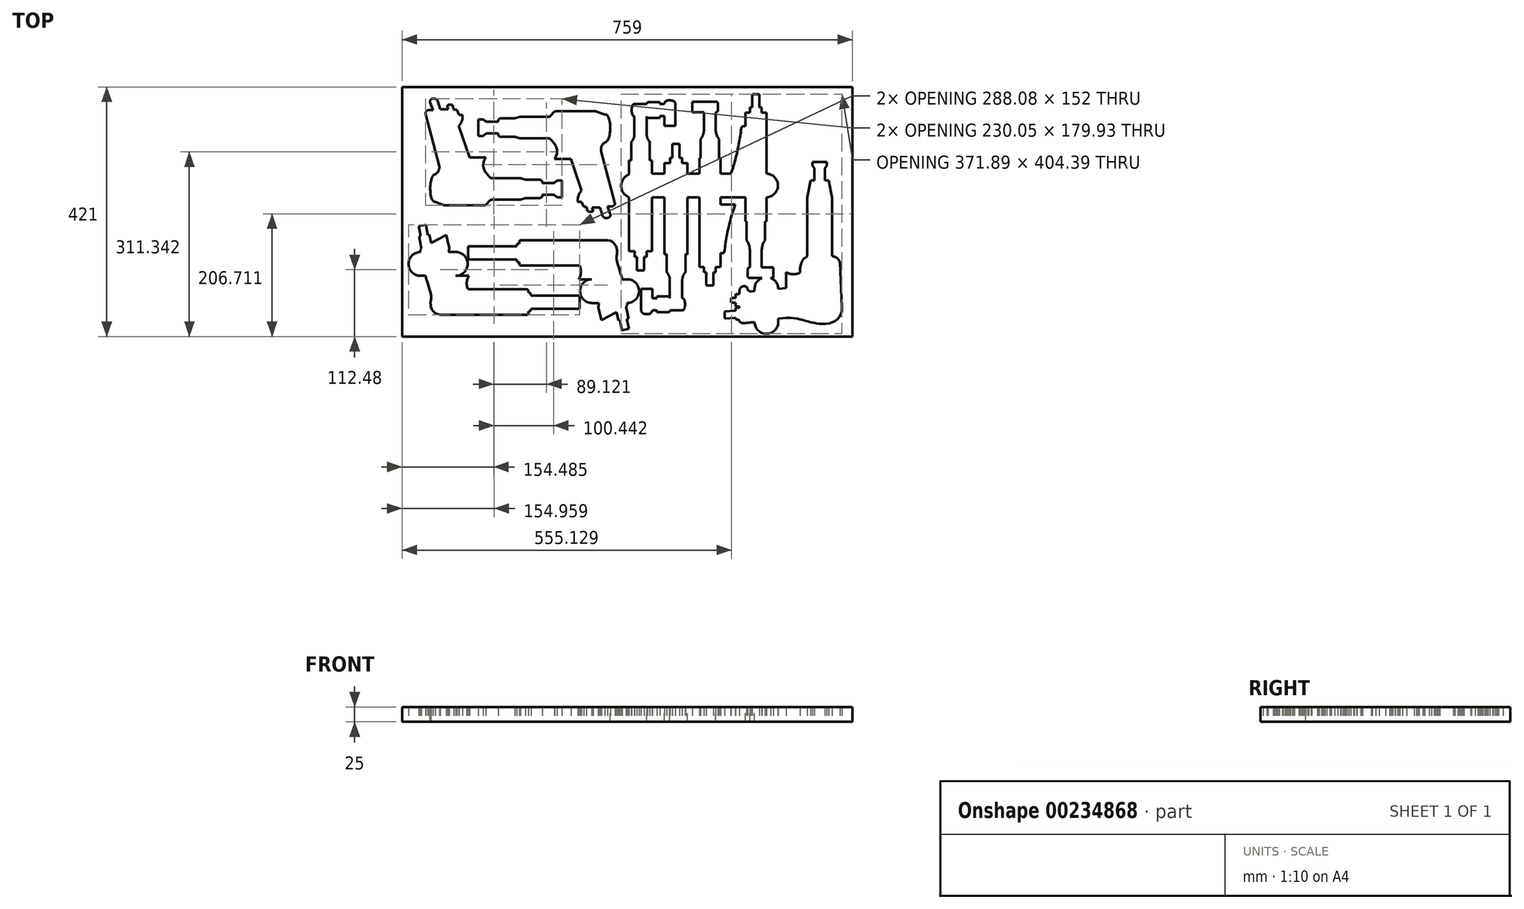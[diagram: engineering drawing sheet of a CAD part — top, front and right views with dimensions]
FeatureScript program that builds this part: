
annotation { "Feature Type Name" : "Feature", "Feature Type Description" : "" }
export const myFeature = defineFeature(function(context is Context, id is Id, definition is map)
    precondition{}
    {
        {
            var Q0;
            Q0=qCreatedBy(makeId("Top.planeOp"),FACE);
            var sketch = newSketch(context, id + "F0", { "sketchPlane" : qUnion([Q0])});
            skLineSegment(sketch, "E0.bottom", {"start": v(0, 0) * mm, "end": v(759, 0) * mm});
            skLineSegment(sketch, "E0.top", {"start": v(0, 421) * mm, "end": v(759, 421) * mm});
            skLineSegment(sketch, "E0.left", {"start": v(0, 0) * mm, "end": v(0, 421) * mm});
            skLineSegment(sketch, "E0.right", {"start": v(759, 0) * mm, "end": v(759, 421) * mm});
            skLineSegment(sketch, "E1", {"start": v(111, 79.48) * mm, "end": v(210, 79.48) * mm});
            skLineSegment(sketch, "E2", {"start": v(213, 76.48) * mm, "end": v(213, 73.79) * mm});
            skLineSegment(sketch, "E3", {"start": v(213, 73.79) * mm, "end": v(214, 73.79) * mm});
            skLineSegment(sketch, "E4", {"start": v(217, 70.79) * mm, "end": v(217, 68.98) * mm});
            skLineSegment(sketch, "E5", {"start": v(217, 68.98) * mm, "end": v(299, 68.98) * mm});
            skLineSegment(sketch, "E6", {"start": v(299, 68.98) * mm, "end": v(299, 57.98) * mm});
            skPoint(sketch, "E7.visualSharp", {"position": v(217, 73.79) * mm});
            skArc(sketch, "E7.filletArc", {"start": v(217, 70.79) * mm, "mid": v(216.12, 72.91) * mm, "end": v(214, 73.79) * mm});
            skPoint(sketch, "E8.visualSharp", {"position": v(213, 79.48) * mm});
            skArc(sketch, "E8.filletArc", {"start": v(213, 76.48) * mm, "mid": v(212.12, 78.6) * mm, "end": v(210, 79.48) * mm});
            skLineSegment(sketch, "E9", {"start": v(299, 57.98) * mm, "end": v(48, 57.98) * mm, "construction": true});
            skLineSegment(sketch, "E10.MirrorCS", {"start": v(217, 45.17) * mm, "end": v(217, 46.98) * mm});
            skLineSegment(sketch, "E11.MirrorCS", {"start": v(213, 39.48) * mm, "end": v(213, 42.17) * mm});
            skLineSegment(sketch, "E12.MirrorCS", {"start": v(213, 42.17) * mm, "end": v(214, 42.17) * mm});
            skArc(sketch, "E13.MirrorCS", {"start": v(213, 39.48) * mm, "mid": v(212.12, 37.36) * mm, "end": v(210, 36.48) * mm});
            skArc(sketch, "E14.MirrorCS", {"start": v(217, 45.17) * mm, "mid": v(216.12, 43.05) * mm, "end": v(214, 42.17) * mm});
            skPoint(sketch, "E15.MirrorP", {"position": v(213, 36.48) * mm});
            skLineSegment(sketch, "E16.MirrorCS", {"start": v(217, 46.98) * mm, "end": v(299, 46.98) * mm});
            skPoint(sketch, "E17.MirrorP", {"position": v(217, 42.17) * mm});
            skLineSegment(sketch, "E18.MirrorCS", {"start": v(111, 36.48) * mm, "end": v(210, 36.48) * mm});
            skLineSegment(sketch, "E19.MirrorCS", {"start": v(299, 46.98) * mm, "end": v(299, 57.98) * mm});
            skArc(sketch, "E20", {"start": v(111, 79.48) * mm, "mid": v(108.94, 91.17) * mm, "end": v(112.55, 102.48) * mm});
            skLineSegment(sketch, "E21", {"start": v(112.55, 102.48) * mm, "end": v(90.55, 102.48) * mm});
            skFitSpline(sketch, "E22", {"points": [v(90.55, 102.48) * mm, v(79.76, 149.3) * mm], "startDerivative": vector(-34.88, 29.55) * mm, "endDerivative": vector(11.44, 42.2) * mm});
            skLineSegment(sketch, "E23", {"start": v(111, 36.48) * mm, "end": v(64, 36.48) * mm});
            skFitSpline(sketch, "E24", {"points": [v(64, 36.48) * mm, v(48, 57.98) * mm, v(49, 67.48) * mm, v(30.64, 145.48) * mm], "startDerivative": vector(-146.18, 22.93) * mm, "endDerivative": vector(-15.62, 185.49) * mm});
            skLineSegment(sketch, "E25", {"start": v(30.64, 145.48) * mm, "end": v(32.76, 148.18) * mm});
            skLineSegment(sketch, "E26", {"start": v(48.76, 157.77) * mm, "end": v(74.25, 171.3) * mm});
            skLineSegment(sketch, "E27", {"start": v(74.25, 171.3) * mm, "end": v(79.76, 149.3) * mm});
            skLineSegment(sketch, "E28", {"start": v(28.24, 186.22) * mm, "end": v(40.02, 188.48) * mm});
            skLineSegment(sketch, "E29", {"start": v(40.02, 188.48) * mm, "end": v(43.32, 171.48) * mm});
            skLineSegment(sketch, "E30", {"start": v(43.32, 171.48) * mm, "end": v(46, 172) * mm});
            skLineSegment(sketch, "E31", {"start": v(46, 172) * mm, "end": v(48.76, 157.77) * mm});
            skLineSegment(sketch, "E32", {"start": v(28.24, 186.22) * mm, "end": v(31.5, 169.21) * mm});
            skLineSegment(sketch, "E33", {"start": v(31.5, 169.21) * mm, "end": v(28.83, 168.7) * mm});
            skLineSegment(sketch, "E34", {"start": v(28.83, 168.7) * mm, "end": v(32.76, 148.18) * mm});
            skLineSegment(sketch, "E35", {"start": v(28.83, 168.7) * mm, "end": v(43.32, 171.48) * mm, "construction": true});
            skLineSegment(sketch, "E36", {"start": v(49, 67.48) * mm, "end": v(49, 95.92) * mm, "construction": true});
            skLineSegment(sketch, "E37", {"start": v(49, 95.92) * mm, "end": v(49, 42.53) * mm, "construction": true});
            skLineSegment(sketch, "E38", {"start": v(299.36, 119.52) * mm, "end": v(200.36, 119.52) * mm});
            skLineSegment(sketch, "E39", {"start": v(197.36, 122.52) * mm, "end": v(197.36, 125.22) * mm});
            skLineSegment(sketch, "E40", {"start": v(197.36, 125.22) * mm, "end": v(196.36, 125.22) * mm});
            skLineSegment(sketch, "E41", {"start": v(193.36, 128.22) * mm, "end": v(193.36, 130.02) * mm});
            skLineSegment(sketch, "E42", {"start": v(193.36, 130.02) * mm, "end": v(111.36, 130.02) * mm});
            skLineSegment(sketch, "E43", {"start": v(111.36, 130.02) * mm, "end": v(111.36, 141.02) * mm});
            skPoint(sketch, "E44.visualSharp", {"position": v(193.36, 125.22) * mm});
            skArc(sketch, "E44.filletArc", {"start": v(193.36, 128.22) * mm, "mid": v(194.24, 126.1) * mm, "end": v(196.36, 125.22) * mm});
            skPoint(sketch, "E45.visualSharp", {"position": v(197.36, 119.52) * mm});
            skArc(sketch, "E45.filletArc", {"start": v(197.36, 122.52) * mm, "mid": v(198.24, 120.4) * mm, "end": v(200.36, 119.52) * mm});
            skLineSegment(sketch, "E46", {"start": v(111.36, 141.02) * mm, "end": v(362.36, 141.02) * mm, "construction": true});
            skLineSegment(sketch, "E47.MirrorCS", {"start": v(193.36, 153.83) * mm, "end": v(193.36, 152.02) * mm});
            skLineSegment(sketch, "E48.MirrorCS", {"start": v(197.36, 159.52) * mm, "end": v(197.36, 156.83) * mm});
            skLineSegment(sketch, "E49.MirrorCS", {"start": v(197.36, 156.83) * mm, "end": v(196.36, 156.83) * mm});
            skArc(sketch, "E50.MirrorCS", {"start": v(197.36, 159.52) * mm, "mid": v(198.24, 161.65) * mm, "end": v(200.36, 162.52) * mm});
            skArc(sketch, "E51.MirrorCS", {"start": v(193.36, 153.83) * mm, "mid": v(194.24, 155.95) * mm, "end": v(196.36, 156.83) * mm});
            skLineSegment(sketch, "E52.MirrorCS", {"start": v(193.36, 152.02) * mm, "end": v(111.36, 152.02) * mm});
            skPoint(sketch, "E53.MirrorP", {"position": v(193.36, 156.83) * mm});
            skLineSegment(sketch, "E54.MirrorCS", {"start": v(299.36, 162.52) * mm, "end": v(200.36, 162.52) * mm});
            skLineSegment(sketch, "E55.MirrorCS", {"start": v(111.36, 152.02) * mm, "end": v(111.36, 141.02) * mm});
            skArc(sketch, "E56", {"start": v(299.36, 119.52) * mm, "mid": v(301.42, 107.83) * mm, "end": v(297.8, 96.52) * mm});
            skLineSegment(sketch, "E57", {"start": v(297.8, 96.52) * mm, "end": v(319.8, 96.52) * mm});
            skFitSpline(sketch, "E58", {"points": [v(319.8, 96.52) * mm, v(330.6, 49.7) * mm], "startDerivative": vector(34.88, -29.55) * mm, "endDerivative": vector(-11.44, -42.2) * mm});
            skLineSegment(sketch, "E59", {"start": v(299.36, 162.52) * mm, "end": v(346.36, 162.52) * mm});
            skFitSpline(sketch, "E60", {"points": [v(346.36, 162.52) * mm, v(362.36, 141.02) * mm, v(361.36, 131.52) * mm, v(379.72, 53.52) * mm], "startDerivative": vector(146.18, -22.93) * mm, "endDerivative": vector(15.62, -185.49) * mm});
            skLineSegment(sketch, "E61", {"start": v(379.72, 53.52) * mm, "end": v(377.6, 50.82) * mm});
            skLineSegment(sketch, "E62", {"start": v(361.6, 41.24) * mm, "end": v(336.11, 27.7) * mm});
            skLineSegment(sketch, "E63", {"start": v(336.11, 27.7) * mm, "end": v(330.6, 49.7) * mm});
            skLineSegment(sketch, "E64", {"start": v(382.12, 12.79) * mm, "end": v(370.34, 10.52) * mm});
            skLineSegment(sketch, "E65", {"start": v(370.34, 10.52) * mm, "end": v(367.04, 27.52) * mm});
            skLineSegment(sketch, "E66", {"start": v(367.04, 27.52) * mm, "end": v(364.36, 27) * mm});
            skLineSegment(sketch, "E67", {"start": v(364.36, 27) * mm, "end": v(361.6, 41.24) * mm});
            skLineSegment(sketch, "E68", {"start": v(382.12, 12.79) * mm, "end": v(378.86, 29.79) * mm});
            skLineSegment(sketch, "E69", {"start": v(378.86, 29.79) * mm, "end": v(381.54, 30.3) * mm});
            skLineSegment(sketch, "E70", {"start": v(381.54, 30.3) * mm, "end": v(377.6, 50.82) * mm});
            skLineSegment(sketch, "E71", {"start": v(381.54, 30.3) * mm, "end": v(367.04, 27.52) * mm, "construction": true});
            skLineSegment(sketch, "E72", {"start": v(361.36, 131.52) * mm, "end": v(361.36, 103.09) * mm, "construction": true});
            skLineSegment(sketch, "E73", {"start": v(361.36, 103.09) * mm, "end": v(361.36, 156.48) * mm, "construction": true});
            skLineSegment(sketch, "E74", {"start": v(325.7, 379.95) * mm, "end": v(259.34, 379.95) * mm});
            skLineSegment(sketch, "E75", {"start": v(255.51, 378.17) * mm, "end": v(250.63, 372.35) * mm});
            skLineSegment(sketch, "E76", {"start": v(246.8, 370.56) * mm, "end": v(198.39, 370.56) * mm});
            skLineSegment(sketch, "E77", {"start": v(198.39, 370.56) * mm, "end": v(190.27, 368) * mm});
            skLineSegment(sketch, "E78", {"start": v(190.27, 368) * mm, "end": v(166.77, 368) * mm});
            skLineSegment(sketch, "E79", {"start": v(161.77, 363) * mm, "end": v(161.77, 362.07) * mm});
            skLineSegment(sketch, "E80", {"start": v(161.77, 362.07) * mm, "end": v(143.75, 362.07) * mm});
            skLineSegment(sketch, "E81", {"start": v(140.54, 363.24) * mm, "end": v(138.2, 365.2) * mm});
            skLineSegment(sketch, "E82", {"start": v(134.99, 366.37) * mm, "end": v(128.58, 366.37) * mm});
            skLineSegment(sketch, "E83", {"start": v(128.58, 366.37) * mm, "end": v(128.58, 352.34) * mm});
            skLineSegment(sketch, "E84", {"start": v(128.58, 352.34) * mm, "end": v(350.7, 352.34) * mm, "construction": true});
            skLineSegment(sketch, "E85", {"start": v(327.34, 379.67) * mm, "end": v(342.03, 374.55) * mm});
            skLineSegment(sketch, "E86.MirrorCS", {"start": v(128.58, 338.3) * mm, "end": v(128.58, 352.34) * mm});
            skLineSegment(sketch, "E87.MirrorCS", {"start": v(134.99, 338.3) * mm, "end": v(128.58, 338.3) * mm});
            skLineSegment(sketch, "E88.MirrorCS", {"start": v(140.54, 341.43) * mm, "end": v(138.2, 339.48) * mm});
            skLineSegment(sketch, "E89.MirrorCS", {"start": v(161.77, 342.6) * mm, "end": v(143.75, 342.6) * mm});
            skLineSegment(sketch, "E90.MirrorCS", {"start": v(161.77, 341.68) * mm, "end": v(161.77, 342.6) * mm});
            skLineSegment(sketch, "E91.MirrorCS", {"start": v(190.27, 336.68) * mm, "end": v(166.77, 336.68) * mm});
            skLineSegment(sketch, "E92.MirrorCS", {"start": v(198.39, 334.1) * mm, "end": v(190.27, 336.68) * mm});
            skLineSegment(sketch, "E93.MirrorCS", {"start": v(246.8, 334.1) * mm, "end": v(198.39, 334.1) * mm});
            skLineSegment(sketch, "E94.MirrorCS", {"start": v(257.01, 324.72) * mm, "end": v(250.63, 332.32) * mm});
            skArc(sketch, "E95", {"start": v(257.01, 324.72) * mm, "mid": v(261.18, 312.01) * mm, "end": v(256.9, 299.34) * mm});
            skLineSegment(sketch, "E96", {"start": v(256.9, 299.34) * mm, "end": v(284.3, 299.34) * mm});
            skLineSegment(sketch, "E97", {"start": v(284.3, 299.34) * mm, "end": v(302.62, 246.15) * mm});
            skArc(sketch, "E98", {"start": v(302.62, 246.15) * mm, "mid": v(297.24, 237.45) * mm, "end": v(296.27, 227.26) * mm});
            skLineSegment(sketch, "E99", {"start": v(358.47, 225.86) * mm, "end": v(335.71, 312.38) * mm});
            skArc(sketch, "E100", {"start": v(335.71, 312.38) * mm, "mid": v(336.3, 321.05) * mm, "end": v(342.03, 327.6) * mm});
            skLineSegment(sketch, "E101", {"start": v(342.03, 327.6) * mm, "end": v(342.03, 374.55) * mm, "construction": true});
            skFitSpline(sketch, "E102", {"points": [v(342.03, 327.6) * mm, v(342.03, 374.55) * mm], "startDerivative": vector(32.61, 0) * mm, "endDerivative": vector(-36.84, 0) * mm});
            skPoint(sketch, "E103.visualSharp", {"position": v(161.77, 336.68) * mm});
            skArc(sketch, "E103.filletArc", {"start": v(161.77, 341.68) * mm, "mid": v(163.23, 338.15) * mm, "end": v(166.77, 336.68) * mm});
            skPoint(sketch, "E104.visualSharp", {"position": v(161.77, 368) * mm});
            skArc(sketch, "E104.filletArc", {"start": v(166.77, 368) * mm, "mid": v(163.23, 366.53) * mm, "end": v(161.77, 363) * mm});
            skPoint(sketch, "E105.visualSharp", {"position": v(141.93, 342.6) * mm});
            skArc(sketch, "E105.filletArc", {"start": v(143.75, 342.6) * mm, "mid": v(142.04, 342.3) * mm, "end": v(140.54, 341.43) * mm});
            skPoint(sketch, "E106.visualSharp", {"position": v(136.8, 338.3) * mm});
            skArc(sketch, "E106.filletArc", {"start": v(134.99, 338.3) * mm, "mid": v(136.7, 338.6) * mm, "end": v(138.2, 339.48) * mm});
            skPoint(sketch, "E107.visualSharp", {"position": v(141.93, 362.07) * mm});
            skArc(sketch, "E107.filletArc", {"start": v(140.54, 363.24) * mm, "mid": v(142.04, 362.37) * mm, "end": v(143.75, 362.07) * mm});
            skPoint(sketch, "E108.visualSharp", {"position": v(136.8, 366.37) * mm});
            skArc(sketch, "E108.filletArc", {"start": v(138.2, 365.2) * mm, "mid": v(136.7, 366.06) * mm, "end": v(134.99, 366.37) * mm});
            skPoint(sketch, "E109.visualSharp", {"position": v(257.01, 379.95) * mm});
            skArc(sketch, "E109.filletArc", {"start": v(259.34, 379.95) * mm, "mid": v(257.23, 379.48) * mm, "end": v(255.51, 378.17) * mm});
            skPoint(sketch, "E110.visualSharp", {"position": v(249.13, 370.56) * mm});
            skArc(sketch, "E110.filletArc", {"start": v(246.8, 370.56) * mm, "mid": v(248.92, 371.03) * mm, "end": v(250.63, 372.35) * mm});
            skPoint(sketch, "E111.visualSharp", {"position": v(249.13, 334.1) * mm});
            skArc(sketch, "E111.filletArc", {"start": v(250.63, 332.32) * mm, "mid": v(248.92, 333.64) * mm, "end": v(246.8, 334.1) * mm});
            skPoint(sketch, "E112.visualSharp", {"position": v(326.54, 379.95) * mm});
            skArc(sketch, "E112.filletArc", {"start": v(327.34, 379.67) * mm, "mid": v(326.53, 379.88) * mm, "end": v(325.7, 379.95) * mm});
            skLineSegment(sketch, "E113", {"start": v(296.27, 227.26) * mm, "end": v(302.12, 227.26) * mm});
            skLineSegment(sketch, "E114", {"start": v(302.12, 227.26) * mm, "end": v(305.95, 218.52) * mm});
            skLineSegment(sketch, "E115", {"start": v(305.95, 218.52) * mm, "end": v(310.7, 218.52) * mm});
            skLineSegment(sketch, "E116", {"start": v(310.7, 218.52) * mm, "end": v(312.74, 212.03) * mm});
            skLineSegment(sketch, "E117", {"start": v(314.64, 210.63) * mm, "end": v(319.79, 210.63) * mm});
            skLineSegment(sketch, "E118", {"start": v(321.71, 213.17) * mm, "end": v(320.4, 217.85) * mm});
            skLineSegment(sketch, "E119", {"start": v(320.4, 217.85) * mm, "end": v(333.71, 217.85) * mm});
            skLineSegment(sketch, "E120", {"start": v(333.71, 217.85) * mm, "end": v(338.25, 203.51) * mm});
            skLineSegment(sketch, "E121", {"start": v(343.02, 200.02) * mm, "end": v(346.05, 200.02) * mm});
            skLineSegment(sketch, "E122", {"start": v(350.77, 206.68) * mm, "end": v(346.2, 219.59) * mm});
            skLineSegment(sketch, "E123", {"start": v(346.2, 219.59) * mm, "end": v(353.63, 219.59) * mm});
            skPoint(sketch, "E124.visualSharp", {"position": v(360.12, 219.59) * mm});
            skArc(sketch, "E124.filletArc", {"start": v(353.63, 219.59) * mm, "mid": v(357.6, 221.54) * mm, "end": v(358.47, 225.86) * mm});
            skPoint(sketch, "E125.visualSharp", {"position": v(353.12, 200.02) * mm});
            skArc(sketch, "E125.filletArc", {"start": v(346.05, 200.02) * mm, "mid": v(350.13, 202.13) * mm, "end": v(350.77, 206.68) * mm});
            skPoint(sketch, "E126.visualSharp", {"position": v(339.35, 200.02) * mm});
            skArc(sketch, "E126.filletArc", {"start": v(338.25, 203.51) * mm, "mid": v(340.06, 200.99) * mm, "end": v(343.02, 200.02) * mm});
            skPoint(sketch, "E127.visualSharp", {"position": v(322.43, 210.63) * mm});
            skArc(sketch, "E127.filletArc", {"start": v(319.79, 210.63) * mm, "mid": v(321.38, 211.42) * mm, "end": v(321.71, 213.17) * mm});
            skPoint(sketch, "E128.visualSharp", {"position": v(313.18, 210.63) * mm});
            skArc(sketch, "E128.filletArc", {"start": v(312.74, 212.03) * mm, "mid": v(313.46, 211.01) * mm, "end": v(314.64, 210.63) * mm});
            skLineSegment(sketch, "E129", {"start": v(72.4, 221.38) * mm, "end": v(138.75, 221.38) * mm});
            skLineSegment(sketch, "E130", {"start": v(142.58, 223.16) * mm, "end": v(147.46, 228.98) * mm});
            skLineSegment(sketch, "E131", {"start": v(151.29, 230.76) * mm, "end": v(199.7, 230.76) * mm});
            skLineSegment(sketch, "E132", {"start": v(199.7, 230.76) * mm, "end": v(207.83, 233.34) * mm});
            skLineSegment(sketch, "E133", {"start": v(207.83, 233.34) * mm, "end": v(231.33, 233.34) * mm});
            skLineSegment(sketch, "E134", {"start": v(236.33, 238.34) * mm, "end": v(236.33, 239.26) * mm});
            skLineSegment(sketch, "E135", {"start": v(236.33, 239.26) * mm, "end": v(254.34, 239.26) * mm});
            skLineSegment(sketch, "E136", {"start": v(257.55, 238.1) * mm, "end": v(259.89, 236.13) * mm});
            skLineSegment(sketch, "E137", {"start": v(263.1, 234.96) * mm, "end": v(269.5, 234.96) * mm});
            skLineSegment(sketch, "E138", {"start": v(269.5, 234.96) * mm, "end": v(269.5, 249) * mm});
            skLineSegment(sketch, "E139", {"start": v(269.5, 249) * mm, "end": v(47.38, 249) * mm, "construction": true});
            skLineSegment(sketch, "E140", {"start": v(70.75, 221.65) * mm, "end": v(56.06, 226.78) * mm});
            skLineSegment(sketch, "E141.MirrorCS", {"start": v(269.5, 263.02) * mm, "end": v(269.5, 249) * mm});
            skLineSegment(sketch, "E142.MirrorCS", {"start": v(263.1, 263.02) * mm, "end": v(269.5, 263.02) * mm});
            skLineSegment(sketch, "E143.MirrorCS", {"start": v(257.55, 259.9) * mm, "end": v(259.89, 261.85) * mm});
            skLineSegment(sketch, "E144.MirrorCS", {"start": v(236.33, 258.72) * mm, "end": v(254.34, 258.72) * mm});
            skLineSegment(sketch, "E145.MirrorCS", {"start": v(236.33, 259.65) * mm, "end": v(236.33, 258.72) * mm});
            skLineSegment(sketch, "E146.MirrorCS", {"start": v(207.83, 264.65) * mm, "end": v(231.33, 264.65) * mm});
            skLineSegment(sketch, "E147.MirrorCS", {"start": v(199.7, 267.22) * mm, "end": v(207.83, 264.65) * mm});
            skLineSegment(sketch, "E148.MirrorCS", {"start": v(151.29, 267.22) * mm, "end": v(199.7, 267.22) * mm});
            skLineSegment(sketch, "E149.MirrorCS", {"start": v(141.08, 276.6) * mm, "end": v(147.46, 269) * mm});
            skArc(sketch, "E150", {"start": v(141.08, 276.6) * mm, "mid": v(136.91, 289.32) * mm, "end": v(141.18, 302) * mm});
            skLineSegment(sketch, "E151", {"start": v(141.18, 302) * mm, "end": v(113.8, 302) * mm});
            skLineSegment(sketch, "E152", {"start": v(113.8, 302) * mm, "end": v(95.47, 355.18) * mm});
            skArc(sketch, "E153", {"start": v(95.47, 355.18) * mm, "mid": v(100.85, 363.88) * mm, "end": v(101.83, 374.06) * mm});
            skLineSegment(sketch, "E154", {"start": v(39.62, 375.47) * mm, "end": v(62.38, 288.95) * mm});
            skArc(sketch, "E155", {"start": v(62.38, 288.95) * mm, "mid": v(61.79, 280.28) * mm, "end": v(56.06, 273.73) * mm});
            skLineSegment(sketch, "E156", {"start": v(56.06, 273.73) * mm, "end": v(56.06, 226.78) * mm, "construction": true});
            skFitSpline(sketch, "E157", {"points": [v(56.06, 273.73) * mm, v(56.06, 226.78) * mm], "startDerivative": vector(-32.61, 0) * mm, "endDerivative": vector(36.84, 0) * mm});
            skPoint(sketch, "E158.visualSharp", {"position": v(236.33, 264.65) * mm});
            skArc(sketch, "E158.filletArc", {"start": v(236.33, 259.65) * mm, "mid": v(234.86, 263.18) * mm, "end": v(231.33, 264.65) * mm});
            skPoint(sketch, "E159.visualSharp", {"position": v(236.33, 233.34) * mm});
            skArc(sketch, "E159.filletArc", {"start": v(231.33, 233.34) * mm, "mid": v(234.86, 234.8) * mm, "end": v(236.33, 238.34) * mm});
            skPoint(sketch, "E160.visualSharp", {"position": v(256.16, 258.72) * mm});
            skArc(sketch, "E160.filletArc", {"start": v(254.34, 258.72) * mm, "mid": v(256.05, 259.02) * mm, "end": v(257.55, 259.9) * mm});
            skPoint(sketch, "E161.visualSharp", {"position": v(261.28, 263.02) * mm});
            skArc(sketch, "E161.filletArc", {"start": v(263.1, 263.02) * mm, "mid": v(261.4, 262.72) * mm, "end": v(259.89, 261.85) * mm});
            skPoint(sketch, "E162.visualSharp", {"position": v(256.16, 239.26) * mm});
            skArc(sketch, "E162.filletArc", {"start": v(257.55, 238.1) * mm, "mid": v(256.05, 238.96) * mm, "end": v(254.34, 239.26) * mm});
            skPoint(sketch, "E163.visualSharp", {"position": v(261.28, 234.96) * mm});
            skArc(sketch, "E163.filletArc", {"start": v(259.89, 236.13) * mm, "mid": v(261.4, 235.26) * mm, "end": v(263.1, 234.96) * mm});
            skPoint(sketch, "E164.visualSharp", {"position": v(141.08, 221.38) * mm});
            skArc(sketch, "E164.filletArc", {"start": v(138.75, 221.38) * mm, "mid": v(140.86, 221.84) * mm, "end": v(142.58, 223.16) * mm});
            skPoint(sketch, "E165.visualSharp", {"position": v(148.96, 230.76) * mm});
            skArc(sketch, "E165.filletArc", {"start": v(151.29, 230.76) * mm, "mid": v(149.17, 230.3) * mm, "end": v(147.46, 228.98) * mm});
            skPoint(sketch, "E166.visualSharp", {"position": v(148.96, 267.22) * mm});
            skArc(sketch, "E166.filletArc", {"start": v(147.46, 269) * mm, "mid": v(149.17, 267.69) * mm, "end": v(151.29, 267.22) * mm});
            skPoint(sketch, "E167.visualSharp", {"position": v(71.55, 221.38) * mm});
            skArc(sketch, "E167.filletArc", {"start": v(70.75, 221.65) * mm, "mid": v(71.56, 221.45) * mm, "end": v(72.4, 221.38) * mm});
            skLineSegment(sketch, "E168", {"start": v(101.83, 374.06) * mm, "end": v(95.97, 374.06) * mm});
            skLineSegment(sketch, "E169", {"start": v(95.97, 374.06) * mm, "end": v(92.14, 382.8) * mm});
            skLineSegment(sketch, "E170", {"start": v(92.14, 382.8) * mm, "end": v(87.4, 382.8) * mm});
            skLineSegment(sketch, "E171", {"start": v(87.4, 382.8) * mm, "end": v(85.36, 389.3) * mm});
            skLineSegment(sketch, "E172", {"start": v(83.45, 390.7) * mm, "end": v(78.3, 390.7) * mm});
            skLineSegment(sketch, "E173", {"start": v(76.38, 388.16) * mm, "end": v(77.7, 383.48) * mm});
            skLineSegment(sketch, "E174", {"start": v(77.7, 383.48) * mm, "end": v(64.38, 383.48) * mm});
            skLineSegment(sketch, "E175", {"start": v(64.38, 383.48) * mm, "end": v(59.84, 397.82) * mm});
            skLineSegment(sketch, "E176", {"start": v(55.08, 401.3) * mm, "end": v(52.04, 401.3) * mm});
            skLineSegment(sketch, "E177", {"start": v(47.32, 394.64) * mm, "end": v(51.88, 381.74) * mm});
            skLineSegment(sketch, "E178", {"start": v(51.88, 381.74) * mm, "end": v(44.46, 381.74) * mm});
            skPoint(sketch, "E179.visualSharp", {"position": v(37.98, 381.74) * mm});
            skArc(sketch, "E179.filletArc", {"start": v(44.46, 381.74) * mm, "mid": v(40.5, 379.8) * mm, "end": v(39.62, 375.47) * mm});
            skPoint(sketch, "E180.visualSharp", {"position": v(44.97, 401.3) * mm});
            skArc(sketch, "E180.filletArc", {"start": v(52.04, 401.3) * mm, "mid": v(47.96, 399.2) * mm, "end": v(47.32, 394.64) * mm});
            skPoint(sketch, "E181.visualSharp", {"position": v(58.74, 401.3) * mm});
            skArc(sketch, "E181.filletArc", {"start": v(59.84, 397.82) * mm, "mid": v(58.03, 400.34) * mm, "end": v(55.08, 401.3) * mm});
            skPoint(sketch, "E182.visualSharp", {"position": v(75.66, 390.7) * mm});
            skArc(sketch, "E182.filletArc", {"start": v(78.3, 390.7) * mm, "mid": v(76.7, 389.9) * mm, "end": v(76.38, 388.16) * mm});
            skPoint(sketch, "E183.visualSharp", {"position": v(84.92, 390.7) * mm});
            skArc(sketch, "E183.filletArc", {"start": v(85.36, 389.3) * mm, "mid": v(84.63, 390.31) * mm, "end": v(83.45, 390.7) * mm});
            skLineSegment(sketch, "E184", {"start": v(724.47, 135.59) * mm, "end": v(724.47, 233.95) * mm});
            skLineSegment(sketch, "E185", {"start": v(724.47, 233.95) * mm, "end": v(719.05, 263.34) * mm});
            skLineSegment(sketch, "E186", {"start": v(719.05, 263.34) * mm, "end": v(712.44, 263.34) * mm});
            skLineSegment(sketch, "E187", {"start": v(712.44, 263.34) * mm, "end": v(712.44, 284.28) * mm});
            skLineSegment(sketch, "E188", {"start": v(703.71, 294.34) * mm, "end": v(703.71, 21.46) * mm, "construction": true});
            skLineSegment(sketch, "E189", {"start": v(715.5, 294.34) * mm, "end": v(703.71, 294.34) * mm});
            skLineSegment(sketch, "E190", {"start": v(715.5, 294.34) * mm, "end": v(715.5, 287.92) * mm});
            skLineSegment(sketch, "E191", {"start": v(715.5, 287.92) * mm, "end": v(712.44, 284.28) * mm});
            skArc(sketch, "E192", {"start": v(724.47, 135.59) * mm, "mid": v(732.83, 132.24) * mm, "end": v(738.08, 124.93) * mm});
            skLineSegment(sketch, "E193", {"start": v(738.08, 124.93) * mm, "end": v(741.08, 50) * mm});
            skLineSegment(sketch, "E194.MirrorCS", {"start": v(682.95, 135.59) * mm, "end": v(682.95, 233.95) * mm});
            skLineSegment(sketch, "E195.MirrorCS", {"start": v(682.95, 233.95) * mm, "end": v(688.38, 263.34) * mm});
            skLineSegment(sketch, "E196.MirrorCS", {"start": v(688.38, 263.34) * mm, "end": v(694.98, 263.34) * mm});
            skLineSegment(sketch, "E197.MirrorCS", {"start": v(694.98, 263.34) * mm, "end": v(694.98, 284.28) * mm});
            skLineSegment(sketch, "E198.MirrorCS", {"start": v(691.92, 287.92) * mm, "end": v(694.98, 284.28) * mm});
            skLineSegment(sketch, "E199.MirrorCS", {"start": v(691.92, 294.34) * mm, "end": v(691.92, 287.92) * mm});
            skLineSegment(sketch, "E200.MirrorCS", {"start": v(691.92, 294.34) * mm, "end": v(703.71, 294.34) * mm});
            skArc(sketch, "E201", {"start": v(670.63, 107.69) * mm, "mid": v(658.86, 105.14) * mm, "end": v(647.26, 108.36) * mm});
            skLineSegment(sketch, "E202", {"start": v(647.26, 108.36) * mm, "end": v(647.26, 81.45) * mm});
            skLineSegment(sketch, "E203", {"start": v(647.26, 81.45) * mm, "end": v(588.53, 75.8) * mm});
            skArc(sketch, "E204", {"start": v(588.53, 75.8) * mm, "mid": v(583.84, 77.6) * mm, "end": v(581.54, 82.06) * mm});
            skArc(sketch, "E205", {"start": v(580.7, 83.48) * mm, "mid": v(572.74, 83.97) * mm, "end": v(568.61, 77.15) * mm});
            skLineSegment(sketch, "E206", {"start": v(568.61, 77.15) * mm, "end": v(568.61, 71.61) * mm});
            skLineSegment(sketch, "E207", {"start": v(568.61, 71.61) * mm, "end": v(561.9, 71.61) * mm});
            skLineSegment(sketch, "E208", {"start": v(561.9, 71.61) * mm, "end": v(561.9, 65.47) * mm});
            skLineSegment(sketch, "E209", {"start": v(561.9, 65.47) * mm, "end": v(554.64, 65.47) * mm});
            skLineSegment(sketch, "E210", {"start": v(554.64, 65.47) * mm, "end": v(554.64, 57) * mm});
            skLineSegment(sketch, "E211", {"start": v(554.64, 57) * mm, "end": v(561.9, 57) * mm});
            skLineSegment(sketch, "E212", {"start": v(561.9, 57) * mm, "end": v(561.9, 50.72) * mm});
            skLineSegment(sketch, "E213", {"start": v(561.9, 50.72) * mm, "end": v(568.61, 50.72) * mm});
            skLineSegment(sketch, "E214", {"start": v(568.61, 50.72) * mm, "end": v(568.61, 48.4) * mm});
            skLineSegment(sketch, "E215", {"start": v(568.61, 48.4) * mm, "end": v(561.9, 48.4) * mm});
            skLineSegment(sketch, "E216", {"start": v(561.9, 48.4) * mm, "end": v(561.9, 43.66) * mm});
            skLineSegment(sketch, "E217", {"start": v(561.9, 43.66) * mm, "end": v(543.74, 42.29) * mm});
            skLineSegment(sketch, "E218", {"start": v(543.74, 42.29) * mm, "end": v(543.74, 30.12) * mm});
            skLineSegment(sketch, "E219", {"start": v(543.74, 30.12) * mm, "end": v(561.9, 31.5) * mm});
            skLineSegment(sketch, "E220", {"start": v(561.9, 31.5) * mm, "end": v(561.9, 28.77) * mm});
            skPoint(sketch, "E221.visualSharp", {"position": v(581.5, 82.83) * mm});
            skArc(sketch, "E221.filletArc", {"start": v(581.54, 82.06) * mm, "mid": v(581.27, 82.86) * mm, "end": v(580.7, 83.48) * mm});
            skLineSegment(sketch, "E222", {"start": v(561.9, 28.77) * mm, "end": v(561.9, 71.61) * mm, "construction": true});
            skFitSpline(sketch, "E223", {"points": [v(561.9, 28.77) * mm, v(568, 27.22) * mm, v(571.35, 23.34) * mm, v(651.78, 31.5) * mm, v(703.71, 21.46) * mm, v(741.08, 50) * mm], "startDerivative": vector(105.75, -0.47) * mm, "endDerivative": vector(-22.9, 305.2) * mm});
            skFitSpline(sketch, "E224", {"points": [v(670.63, 107.69) * mm, v(676.01, 129.75) * mm, v(682.95, 135.59) * mm], "startDerivative": vector(0, 66.38) * mm, "endDerivative": vector(27.7, 19.38) * mm});
            skLineSegment(sketch, "E225", {"start": v(481, 292.64) * mm, "end": v(481, 139.08) * mm});
            skLineSegment(sketch, "E226", {"start": v(481, 139.08) * mm, "end": v(477.42, 139.08) * mm});
            skLineSegment(sketch, "E227", {"start": v(477.42, 139.08) * mm, "end": v(477.42, 108.5) * mm});
            skLineSegment(sketch, "E228", {"start": v(461.7, 324.9) * mm, "end": v(461.7, 44.05) * mm, "construction": true});
            skLineSegment(sketch, "E229", {"start": v(481, 292.64) * mm, "end": v(471.84, 292.64) * mm});
            skLineSegment(sketch, "E230", {"start": v(471.84, 292.64) * mm, "end": v(471.84, 301.6) * mm});
            skLineSegment(sketch, "E231", {"start": v(471.84, 301.6) * mm, "end": v(467.74, 301.6) * mm});
            skLineSegment(sketch, "E232", {"start": v(467.74, 301.6) * mm, "end": v(467.74, 324.9) * mm});
            skLineSegment(sketch, "E233", {"start": v(467.74, 324.9) * mm, "end": v(461.7, 324.9) * mm});
            skLineSegment(sketch, "E234", {"start": v(472.23, 95.46) * mm, "end": v(472.23, 64.64) * mm});
            skLineSegment(sketch, "E235", {"start": v(472.23, 64.64) * mm, "end": v(472.23, 44.05) * mm, "construction": true});
            skLineSegment(sketch, "E236", {"start": v(451.34, 44.05) * mm, "end": v(472.23, 44.05) * mm});
            skFitSpline(sketch, "E237", {"points": [v(477.42, 108.5) * mm, v(472.23, 95.46) * mm], "startDerivative": vector(-6.48, -7.71) * mm, "endDerivative": vector(0.43, -17.39) * mm});
            skLineSegment(sketch, "E238", {"start": v(476.7, 54.18) * mm, "end": v(403.05, 54.18) * mm, "construction": true});
            skFitSpline(sketch, "E239", {"points": [v(472.23, 64.64) * mm, v(472.23, 44.05) * mm], "startDerivative": vector(17.86, -0.09) * mm, "endDerivative": vector(-18.5, -0.05) * mm});
            skLineSegment(sketch, "E240", {"start": v(451.34, 44.05) * mm, "end": v(450.2, 40.87) * mm});
            skLineSegment(sketch, "E241", {"start": v(450.2, 40.87) * mm, "end": v(429.2, 40.87) * mm});
            skLineSegment(sketch, "E242", {"start": v(429.2, 40.87) * mm, "end": v(429.2, 44.05) * mm});
            skLineSegment(sketch, "E243", {"start": v(429.2, 44.05) * mm, "end": v(421.55, 44.05) * mm});
            skLineSegment(sketch, "E244.MirrorCS", {"start": v(451.34, 64.3) * mm, "end": v(450.2, 67.49) * mm});
            skLineSegment(sketch, "E245.MirrorCS", {"start": v(450.2, 67.49) * mm, "end": v(429.2, 67.49) * mm});
            skLineSegment(sketch, "E246.MirrorCS", {"start": v(429.2, 67.49) * mm, "end": v(429.2, 64.3) * mm});
            skLineSegment(sketch, "E247.MirrorCS", {"start": v(429.2, 64.3) * mm, "end": v(421.55, 64.3) * mm});
            skFitSpline(sketch, "E248", {"points": [v(421.55, 44.05) * mm, v(402.81, 44.05) * mm], "startDerivative": vector(-0.83, -26.9) * mm, "endDerivative": vector(-0.8, 24.2) * mm});
            skLineSegment(sketch, "E249", {"start": v(402.81, 44.05) * mm, "end": v(402.81, 80.56) * mm});
            skLineSegment(sketch, "E250", {"start": v(402.81, 80.56) * mm, "end": v(421.55, 80.56) * mm});
            skLineSegment(sketch, "E251", {"start": v(421.55, 64.3) * mm, "end": v(421.55, 80.56) * mm});
            skLineSegment(sketch, "E252.MirrorCS", {"start": v(451.16, 95.46) * mm, "end": v(451.16, 64.64) * mm});
            skFitSpline(sketch, "E253.MirrorCS", {"points": [v(445.97, 108.5) * mm, v(451.16, 95.46) * mm], "startDerivative": vector(6.48, -7.71) * mm, "endDerivative": vector(-0.43, -17.39) * mm});
            skLineSegment(sketch, "E254.MirrorCS", {"start": v(445.97, 139.08) * mm, "end": v(445.97, 108.5) * mm});
            skLineSegment(sketch, "E255.MirrorCS", {"start": v(442.4, 139.08) * mm, "end": v(445.97, 139.08) * mm});
            skLineSegment(sketch, "E256.MirrorCS", {"start": v(442.4, 292.64) * mm, "end": v(442.4, 139.08) * mm});
            skLineSegment(sketch, "E257.MirrorCS", {"start": v(442.4, 292.64) * mm, "end": v(451.55, 292.64) * mm});
            skLineSegment(sketch, "E258.MirrorCS", {"start": v(451.55, 292.64) * mm, "end": v(451.55, 301.6) * mm});
            skLineSegment(sketch, "E259.MirrorCS", {"start": v(451.55, 301.6) * mm, "end": v(455.66, 301.6) * mm});
            skLineSegment(sketch, "E260.MirrorCS", {"start": v(455.66, 301.6) * mm, "end": v(455.66, 324.9) * mm});
            skLineSegment(sketch, "E261.MirrorCS", {"start": v(455.66, 324.9) * mm, "end": v(461.7, 324.9) * mm});
            skLineSegment(sketch, "E262", {"start": v(382.56, 143.58) * mm, "end": v(382.56, 297.14) * mm});
            skLineSegment(sketch, "E263", {"start": v(382.56, 297.14) * mm, "end": v(386.14, 297.14) * mm});
            skLineSegment(sketch, "E264", {"start": v(386.14, 297.14) * mm, "end": v(386.14, 327.72) * mm});
            skLineSegment(sketch, "E265", {"start": v(401.87, 111.32) * mm, "end": v(401.87, 392.17) * mm, "construction": true});
            skLineSegment(sketch, "E266", {"start": v(382.56, 143.58) * mm, "end": v(391.72, 143.58) * mm});
            skLineSegment(sketch, "E267", {"start": v(391.72, 143.58) * mm, "end": v(391.72, 134.62) * mm});
            skLineSegment(sketch, "E268", {"start": v(391.72, 134.62) * mm, "end": v(395.83, 134.62) * mm});
            skLineSegment(sketch, "E269", {"start": v(395.83, 134.62) * mm, "end": v(395.83, 111.32) * mm});
            skLineSegment(sketch, "E270", {"start": v(395.83, 111.32) * mm, "end": v(401.87, 111.32) * mm});
            skLineSegment(sketch, "E271", {"start": v(391.33, 340.76) * mm, "end": v(391.33, 371.58) * mm});
            skLineSegment(sketch, "E272", {"start": v(391.33, 371.58) * mm, "end": v(391.33, 392.17) * mm, "construction": true});
            skLineSegment(sketch, "E273", {"start": v(412.22, 392.17) * mm, "end": v(391.33, 392.17) * mm});
            skFitSpline(sketch, "E274", {"points": [v(386.14, 327.72) * mm, v(391.33, 340.76) * mm], "startDerivative": vector(6.48, 7.71) * mm, "endDerivative": vector(-0.43, 17.39) * mm});
            skLineSegment(sketch, "E275", {"start": v(386.86, 382.04) * mm, "end": v(460.52, 382.04) * mm, "construction": true});
            skFitSpline(sketch, "E276", {"points": [v(391.33, 371.58) * mm, v(391.33, 392.17) * mm], "startDerivative": vector(-17.86, 0.09) * mm, "endDerivative": vector(18.5, 0.05) * mm});
            skLineSegment(sketch, "E277", {"start": v(412.22, 392.17) * mm, "end": v(413.37, 395.35) * mm});
            skLineSegment(sketch, "E278", {"start": v(413.37, 395.35) * mm, "end": v(434.36, 395.35) * mm});
            skLineSegment(sketch, "E279", {"start": v(434.36, 395.35) * mm, "end": v(434.36, 392.17) * mm});
            skLineSegment(sketch, "E280", {"start": v(434.36, 392.17) * mm, "end": v(442, 392.17) * mm});
            skLineSegment(sketch, "E281.MirrorCS", {"start": v(412.22, 371.91) * mm, "end": v(413.37, 368.73) * mm});
            skLineSegment(sketch, "E282.MirrorCS", {"start": v(413.37, 368.73) * mm, "end": v(434.36, 368.73) * mm});
            skLineSegment(sketch, "E283.MirrorCS", {"start": v(434.36, 368.73) * mm, "end": v(434.36, 371.91) * mm});
            skLineSegment(sketch, "E284.MirrorCS", {"start": v(434.36, 371.91) * mm, "end": v(442, 371.91) * mm});
            skFitSpline(sketch, "E285", {"points": [v(442, 392.17) * mm, v(460.75, 392.17) * mm], "startDerivative": vector(0.83, 26.9) * mm, "endDerivative": vector(0.8, -24.2) * mm});
            skLineSegment(sketch, "E286", {"start": v(460.75, 392.17) * mm, "end": v(460.75, 355.66) * mm});
            skLineSegment(sketch, "E287", {"start": v(460.75, 355.66) * mm, "end": v(442, 355.66) * mm});
            skLineSegment(sketch, "E288", {"start": v(442, 371.91) * mm, "end": v(442, 355.66) * mm});
            skLineSegment(sketch, "E289.MirrorCS", {"start": v(412.4, 340.76) * mm, "end": v(412.4, 371.58) * mm});
            skFitSpline(sketch, "E290.MirrorCS", {"points": [v(417.59, 327.72) * mm, v(412.4, 340.76) * mm], "startDerivative": vector(-6.48, 7.71) * mm, "endDerivative": vector(0.43, 17.39) * mm});
            skLineSegment(sketch, "E291.MirrorCS", {"start": v(417.59, 297.14) * mm, "end": v(417.59, 327.72) * mm});
            skLineSegment(sketch, "E292.MirrorCS", {"start": v(421.17, 297.14) * mm, "end": v(417.59, 297.14) * mm});
            skLineSegment(sketch, "E293.MirrorCS", {"start": v(421.17, 143.58) * mm, "end": v(421.17, 297.14) * mm});
            skLineSegment(sketch, "E294.MirrorCS", {"start": v(421.17, 143.58) * mm, "end": v(412.01, 143.58) * mm});
            skLineSegment(sketch, "E295.MirrorCS", {"start": v(412.01, 143.58) * mm, "end": v(412.01, 134.62) * mm});
            skLineSegment(sketch, "E296.MirrorCS", {"start": v(412.01, 134.62) * mm, "end": v(407.9, 134.62) * mm});
            skLineSegment(sketch, "E297.MirrorCS", {"start": v(407.9, 134.62) * mm, "end": v(407.9, 111.32) * mm});
            skLineSegment(sketch, "E298.MirrorCS", {"start": v(407.9, 111.32) * mm, "end": v(401.87, 111.32) * mm});
            skLineSegment(sketch, "E299", {"start": v(596.07, 408.9) * mm, "end": v(596.07, 98.84) * mm, "construction": true});
            skLineSegment(sketch, "E300", {"start": v(596.07, 408.9) * mm, "end": v(589.92, 408.9) * mm});
            skLineSegment(sketch, "E301", {"start": v(589.92, 408.9) * mm, "end": v(589.92, 386.28) * mm});
            skLineSegment(sketch, "E302", {"start": v(589.92, 386.28) * mm, "end": v(586.13, 386.28) * mm});
            skLineSegment(sketch, "E303", {"start": v(586.13, 386.28) * mm, "end": v(586.13, 377.62) * mm});
            skLineSegment(sketch, "E304", {"start": v(586.13, 377.62) * mm, "end": v(578.3, 377.62) * mm});
            skLineSegment(sketch, "E305", {"start": v(578.3, 377.62) * mm, "end": v(578.3, 354.42) * mm});
            skLineSegment(sketch, "E306", {"start": v(578.3, 354.42) * mm, "end": v(574.62, 354.42) * mm});
            skFitSpline(sketch, "E307", {"points": [v(571.96, 354.42) * mm, v(553.07, 271.98) * mm], "startDerivative": vector(-10.52, -88.27) * mm, "endDerivative": vector(-28.7, -77.75) * mm});
            skArc(sketch, "E308.filletArc", {"start": v(574.62, 354.42) * mm, "mid": v(572.63, 353.67) * mm, "end": v(571.64, 351.79) * mm});
            skLineSegment(sketch, "E309", {"start": v(553.07, 271.98) * mm, "end": v(578.3, 271.98) * mm});
            skLineSegment(sketch, "E310", {"start": v(578.3, 271.98) * mm, "end": v(578.3, 194.2) * mm});
            skLineSegment(sketch, "E311.MirrorCS", {"start": v(606.02, 386.28) * mm, "end": v(606.02, 377.62) * mm});
            skLineSegment(sketch, "E312.MirrorCS", {"start": v(606.02, 377.62) * mm, "end": v(613.84, 377.62) * mm});
            skLineSegment(sketch, "E313.MirrorCS", {"start": v(602.22, 386.28) * mm, "end": v(606.02, 386.28) * mm});
            skLineSegment(sketch, "E314.MirrorCS", {"start": v(613.84, 377.62) * mm, "end": v(613.84, 354.42) * mm});
            skLineSegment(sketch, "E315.MirrorCS", {"start": v(602.22, 408.9) * mm, "end": v(602.22, 386.28) * mm});
            skLineSegment(sketch, "E316.MirrorCS", {"start": v(613.84, 354.42) * mm, "end": v(613.84, 194.2) * mm});
            skLineSegment(sketch, "E317", {"start": v(613.84, 194.2) * mm, "end": v(611.36, 194.2) * mm});
            skLineSegment(sketch, "E318", {"start": v(611.36, 194.2) * mm, "end": v(611.36, 162.08) * mm});
            skFitSpline(sketch, "E319", {"points": [v(611.36, 162.08) * mm, v(605.83, 116.4) * mm], "startDerivative": vector(-20.63, -32.63) * mm, "endDerivative": vector(-1.28, -98.79) * mm});
            skLineSegment(sketch, "E320", {"start": v(605.83, 116.4) * mm, "end": v(625.38, 116.4) * mm});
            skLineSegment(sketch, "E321", {"start": v(625.38, 116.4) * mm, "end": v(625.38, 98.84) * mm});
            skLineSegment(sketch, "E322", {"start": v(625.38, 98.84) * mm, "end": v(585.4, 98.84) * mm});
            skLineSegment(sketch, "E323", {"start": v(582.4, 101.84) * mm, "end": v(582.4, 113.4) * mm});
            skLineSegment(sketch, "E324", {"start": v(585.4, 116.4) * mm, "end": v(586.31, 116.4) * mm});
            skFitSpline(sketch, "E325.MirrorCS", {"points": [v(580.78, 162.08) * mm, v(586.31, 116.4) * mm], "startDerivative": vector(20.63, -32.63) * mm, "endDerivative": vector(1.28, -98.79) * mm});
            skLineSegment(sketch, "E326.MirrorCS", {"start": v(580.78, 194.2) * mm, "end": v(580.78, 162.08) * mm});
            skLineSegment(sketch, "E327.MirrorCS", {"start": v(578.3, 194.2) * mm, "end": v(580.78, 194.2) * mm});
            skPoint(sketch, "E328.visualSharp", {"position": v(582.4, 116.4) * mm});
            skArc(sketch, "E328.filletArc", {"start": v(585.4, 116.4) * mm, "mid": v(583.27, 115.52) * mm, "end": v(582.4, 113.4) * mm});
            skPoint(sketch, "E329.visualSharp", {"position": v(582.4, 98.84) * mm});
            skArc(sketch, "E329.filletArc", {"start": v(582.4, 101.84) * mm, "mid": v(583.27, 99.72) * mm, "end": v(585.4, 98.84) * mm});
            skLineSegment(sketch, "E330.MirrorCS", {"start": v(596.07, 408.9) * mm, "end": v(602.22, 408.9) * mm});
            skLineSegment(sketch, "E331", {"start": v(518.6, 85.93) * mm, "end": v(518.6, 396) * mm, "construction": true});
            skLineSegment(sketch, "E332", {"start": v(518.6, 85.93) * mm, "end": v(524.75, 85.93) * mm});
            skLineSegment(sketch, "E333", {"start": v(524.75, 85.93) * mm, "end": v(524.75, 108.56) * mm});
            skLineSegment(sketch, "E334", {"start": v(524.75, 108.56) * mm, "end": v(528.55, 108.56) * mm});
            skLineSegment(sketch, "E335", {"start": v(528.55, 108.56) * mm, "end": v(528.55, 117.22) * mm});
            skLineSegment(sketch, "E336", {"start": v(528.55, 117.22) * mm, "end": v(536.37, 117.22) * mm});
            skLineSegment(sketch, "E337", {"start": v(536.37, 117.22) * mm, "end": v(536.37, 140.42) * mm});
            skLineSegment(sketch, "E338", {"start": v(536.37, 140.42) * mm, "end": v(540.06, 140.42) * mm});
            skFitSpline(sketch, "E339", {"points": [v(542.71, 140.42) * mm, v(561.6, 222.86) * mm], "startDerivative": vector(10.52, 88.27) * mm, "endDerivative": vector(28.7, 77.75) * mm});
            skArc(sketch, "E340.filletArc", {"start": v(540.06, 140.42) * mm, "mid": v(542.04, 141.17) * mm, "end": v(543.03, 143.05) * mm});
            skLineSegment(sketch, "E341", {"start": v(561.6, 222.86) * mm, "end": v(536.37, 222.86) * mm});
            skLineSegment(sketch, "E342", {"start": v(536.37, 222.86) * mm, "end": v(536.37, 300.64) * mm});
            skLineSegment(sketch, "E343.MirrorCS", {"start": v(508.66, 108.56) * mm, "end": v(508.66, 117.22) * mm});
            skLineSegment(sketch, "E344.MirrorCS", {"start": v(508.66, 117.22) * mm, "end": v(500.83, 117.22) * mm});
            skLineSegment(sketch, "E345.MirrorCS", {"start": v(512.45, 108.56) * mm, "end": v(508.66, 108.56) * mm});
            skLineSegment(sketch, "E346.MirrorCS", {"start": v(500.83, 117.22) * mm, "end": v(500.83, 140.42) * mm});
            skLineSegment(sketch, "E347.MirrorCS", {"start": v(512.45, 85.93) * mm, "end": v(512.45, 108.56) * mm});
            skLineSegment(sketch, "E348.MirrorCS", {"start": v(500.83, 140.42) * mm, "end": v(500.83, 300.64) * mm});
            skLineSegment(sketch, "E349", {"start": v(500.83, 300.64) * mm, "end": v(503.31, 300.64) * mm});
            skLineSegment(sketch, "E350", {"start": v(503.31, 300.64) * mm, "end": v(503.31, 332.76) * mm});
            skFitSpline(sketch, "E351", {"points": [v(503.31, 332.76) * mm, v(508.9, 378.44) * mm], "startDerivative": vector(20.63, 32.63) * mm, "endDerivative": vector(1.28, 98.79) * mm});
            skLineSegment(sketch, "E352", {"start": v(508.9, 378.44) * mm, "end": v(489.3, 378.44) * mm});
            skLineSegment(sketch, "E353", {"start": v(489.3, 378.44) * mm, "end": v(489.3, 396) * mm});
            skLineSegment(sketch, "E354", {"start": v(489.3, 396) * mm, "end": v(529.28, 396) * mm});
            skLineSegment(sketch, "E355", {"start": v(532.28, 393) * mm, "end": v(532.28, 381.44) * mm});
            skLineSegment(sketch, "E356", {"start": v(529.28, 378.44) * mm, "end": v(528.3, 378.44) * mm});
            skFitSpline(sketch, "E357.MirrorCS", {"points": [v(533.9, 332.76) * mm, v(528.3, 378.44) * mm], "startDerivative": vector(-20.63, 32.63) * mm, "endDerivative": vector(-1.28, 98.79) * mm});
            skLineSegment(sketch, "E358.MirrorCS", {"start": v(533.9, 300.64) * mm, "end": v(533.9, 332.76) * mm});
            skLineSegment(sketch, "E359.MirrorCS", {"start": v(536.37, 300.64) * mm, "end": v(533.9, 300.64) * mm});
            skPoint(sketch, "E360.visualSharp", {"position": v(532.28, 378.44) * mm});
            skArc(sketch, "E360.filletArc", {"start": v(529.28, 378.44) * mm, "mid": v(531.4, 379.32) * mm, "end": v(532.28, 381.44) * mm});
            skPoint(sketch, "E361.visualSharp", {"position": v(532.28, 396) * mm});
            skArc(sketch, "E361.filletArc", {"start": v(532.28, 393) * mm, "mid": v(531.4, 395.12) * mm, "end": v(529.28, 396) * mm});
            skLineSegment(sketch, "E362.MirrorCS", {"start": v(518.6, 85.93) * mm, "end": v(512.45, 85.93) * mm});
            skSolve(sketch);
        }
        {
            var Q0;
            Q0 = qSketchRegion(id + "F0", true);
            extrude(context, id + "F1", {"entities" : qUnion([Q0]), "depth" : 25 * mm});
        }
        {
            var Q0;
            Q0=qCreatedBy(makeId("Top.planeOp"),FACE);
            var sketch = newSketch(context, id + "F2", { "sketchPlane" : qUnion([Q0])});
            skLineSegment(sketch, "E363.bottom", {"start": v(389.86, 274.78) * mm, "end": v(613.32, 274.78) * mm});
            skLineSegment(sketch, "E363.top", {"start": v(382.5, 234.78) * mm, "end": v(613.32, 234.78) * mm});
            skLineSegment(sketch, "E364.left", {"start": v(593.97, 80.17) * mm, "end": v(593.97, 24.52) * mm});
            skLineSegment(sketch, "E364.right", {"start": v(633.97, 80.17) * mm, "end": v(633.97, 24.52) * mm});
            skLineSegment(sketch, "E365.bottom", {"start": v(319.8, 96.52) * mm, "end": v(379.44, 96.52) * mm});
            skLineSegment(sketch, "E365.top", {"start": v(319.8, 56.52) * mm, "end": v(379.44, 56.52) * mm});
            skLineSegment(sketch, "E366.bottom", {"start": v(30.92, 142.48) * mm, "end": v(90.55, 142.48) * mm});
            skLineSegment(sketch, "E366.top", {"start": v(30.92, 102.48) * mm, "end": v(90.55, 102.48) * mm});
            skArc(sketch, "E367", {"start": v(90.55, 142.48) * mm, "mid": v(110.55, 122.48) * mm, "end": v(90.55, 102.48) * mm});
            skArc(sketch, "E368", {"start": v(30.92, 102.48) * mm, "mid": v(10.92, 122.48) * mm, "end": v(30.92, 142.48) * mm});
            skArc(sketch, "E369", {"start": v(389.86, 274.78) * mm, "mid": v(369.52, 257.84) * mm, "end": v(382.5, 234.78) * mm});
            skArc(sketch, "E370", {"start": v(613.32, 274.78) * mm, "mid": v(633.32, 254.78) * mm, "end": v(613.32, 234.78) * mm});
            skArc(sketch, "E371", {"start": v(379.44, 96.52) * mm, "mid": v(399.44, 76.52) * mm, "end": v(379.44, 56.52) * mm});
            skArc(sketch, "E372", {"start": v(319.8, 56.52) * mm, "mid": v(299.8, 76.52) * mm, "end": v(319.8, 96.52) * mm});
            skArc(sketch, "E373", {"start": v(633.97, 80.17) * mm, "mid": v(613.97, 100.17) * mm, "end": v(593.97, 80.17) * mm});
            skArc(sketch, "E374", {"start": v(633.97, 24.52) * mm, "mid": v(613.97, 4.52) * mm, "end": v(593.97, 24.52) * mm});
            skSolve(sketch);
        }
        {
            var Q0;
            Q0 = qSketchRegion(id + "F2", true);
            extrude(context, id + "F3", {"entities" : qUnion([Q0]), "operationType" : NewBodyOperationType.REMOVE, "depth" : 25 * mm});
        }
    });
